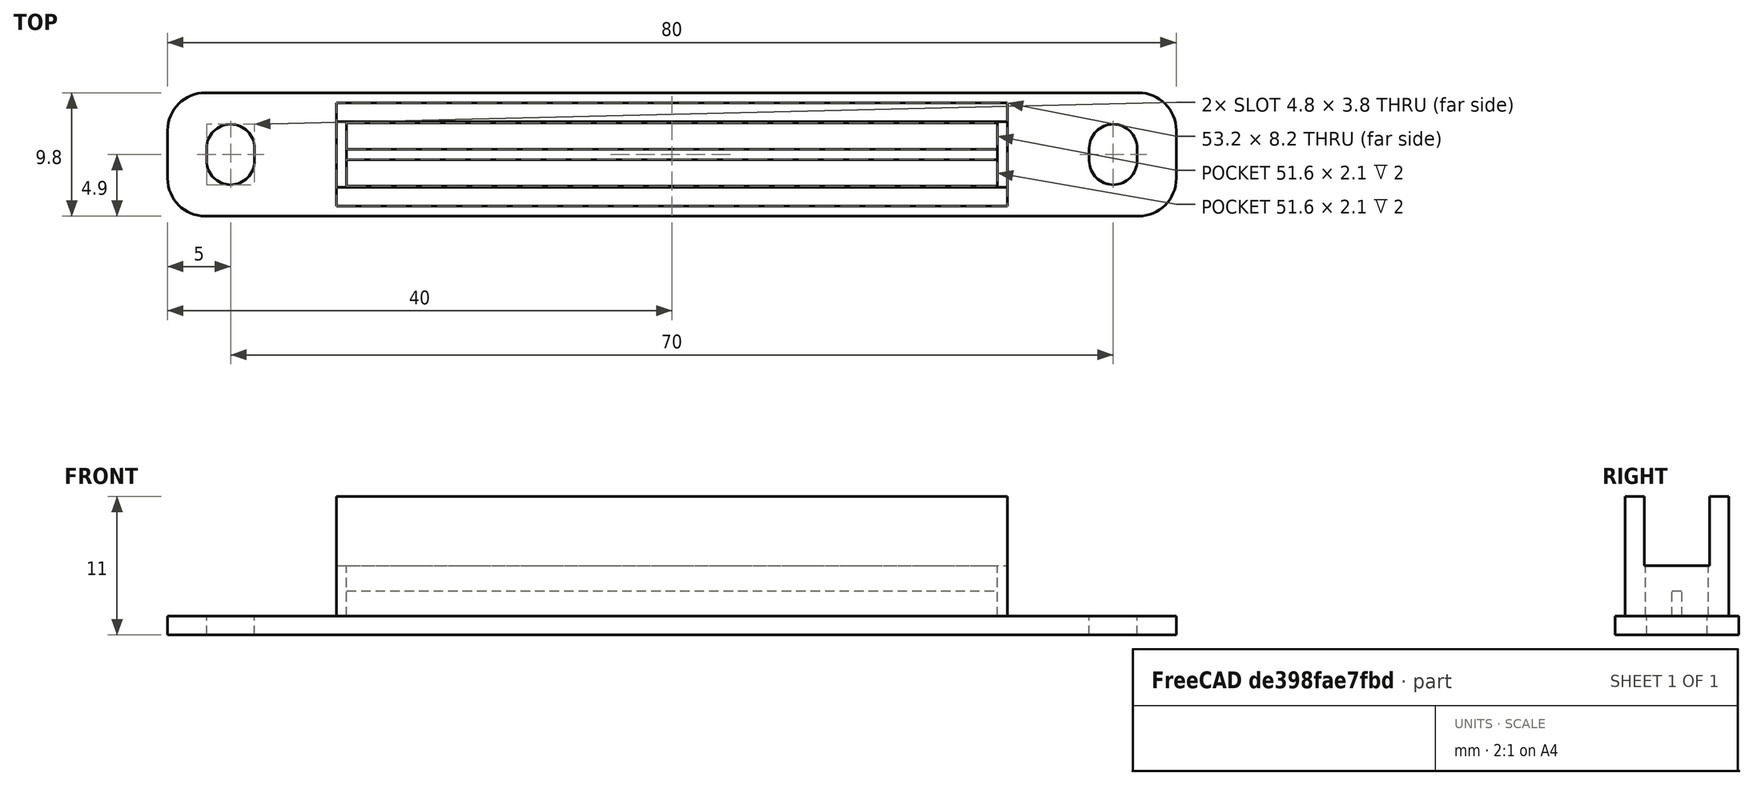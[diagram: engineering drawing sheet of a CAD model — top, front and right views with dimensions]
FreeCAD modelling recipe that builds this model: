
FCSTD DOCUMENT  (FreeCAD 0.19R23578 (Git))
Label: pin_socket_holder
License: All rights reserved
LicenseURL: http://en.wikipedia.org/wiki/All_rights_reserved
objects: Part::Box×6, Part::Cut×3, Part::MultiFuse×3, Spreadsheet::Sheet×2, Part::Cylinder×2, Part::Fillet×1, Part::FeaturePython×1
note: 16 computed .brp shape members not serialized (recipe doc carries the construction recipe); baked Part::Feature solids carry a one-line shape summary decoded from their .brp

FEATURE [Part::Box] Box  label="external cube"
  AttacherType = Attacher::AttachEngine3D
  Height = 11
  Length = 53.2
  Width = 8.2
  expr: Height = <<p>>.external_z
  expr: Width = <<p>>.internal_y + 2 * <<p>>.wall
  expr: Length = <<p>>.internal_x
FEATURE [Spreadsheet::Sheet] Spreadsheet  label="p"
  cells = A1=pin_step; B1(pin_step)==2.5mm; A2=pin_count_y; B2(pin_count_y)=2; A3=pin_count_x; B3(pin_count_x)=20; A4=wall; B4(wall)==1.5mm; A5=external_z; B5(external_z)==11mm; A6=internal_x; B6(internal_x)==pin_count_x * pin_step + 3.2mm; A7=internal_y; B7(internal_y)==pin_step * pin_count_y + 0.2mm; A8=internal_hole_x; B8(internal_hole_x)==pin_count_x * pin_step + 1.6mm; A9=internal_hole_y; B9(internal_hole_y)==pin_step * pin_count_y; A10=internal_hole_z; B10(internal_hole_z)==4mm; A11=hole_middle_extract_y; B11(hole_middle_extract_y)==0.8mm; A12=hole_middle_extract_z; B12(hole_middle_extract_z)==2mm
FEATURE [Part::Box] Box001  label="bottom hole"
  AttacherType = Attacher::AttachEngine3D
  Height = 4
  Length = 51.6
  Placement = pos=(0.8,1.6,1.5) rot=(0,0,1;0rad)
  Width = 5
  expr: Length = <<p>>.internal_hole_x
  expr: Width = <<p>>.internal_hole_y
  expr: Height = <<p>>.internal_hole_z
  expr: .Placement.Base.x = (<<external cube>>.Length - Length) / 2
  expr: .Placement.Base.y = (<<external cube>>.Width - Width) / 2
  expr: .Placement.Base.z = <<p>>.wall
FEATURE [Part::Box] Box002  label="internal_extraction"
  AttacherType = Attacher::AttachEngine3D
  Height = 11
  Length = 53.2
  Placement = pos=(0,1.5,5.5) rot=(0,0,1;0rad)
  Width = 5.2
  expr: Height = <<p>>.external_z
  expr: Length = <<p>>.internal_x
  expr: Width = <<p>>.internal_y
  expr: .Placement.Base.x = (<<external cube>>.Length - Length) / 2
  expr: .Placement.Base.y = (<<external cube>>.Width - Width) / 2
  expr: .Placement.Base.z = <<p>>.wall + <<p>>.internal_hole_z
FEATURE [Part::Box] Box003  label="bottom hole middle extraction"
  AttacherType = Attacher::AttachEngine3D
  Height = 2
  Length = 51.6
  Placement = pos=(0.8,3.7,1.5) rot=(0,0,1;0rad)
  Width = 0.8
  expr: .Placement.Base.z = <<p>>.wall
  expr: .Placement.Base.y = (<<external cube>>.Width - Width) / 2
  expr: .Placement.Base.x = (<<external cube>>.Length - Length) / 2
  expr: Width = <<p>>.hole_middle_extract_y
  expr: Length = <<p>>.internal_hole_x
  expr: Height = <<p>>.hole_middle_extract_z
FEATURE [Part::Cut] Cut003003  label="bottom hole cut"
  Base = -> Box001
  Tool = -> Box003
FEATURE [Part::MultiFuse] Fusion  label="hole fusion"
  Shapes = -> [Box002,Cut003003]
FEATURE [Part::Box] Box008  label="inbetween holes cube001"
  AttacherType = Attacher::AttachEngine3D
  Height = 10
  Length = 3.8
  Placement = pos=(-1.9,0,0) rot=(0,0,1;0rad)
  Width = 1
  expr: Length = <<attach_p>>.attach_hole_r * 2
  expr: .Placement.Base.x = -<<attach_p>>.attach_hole_r
  expr: Width = <<attach_p>>.attach_extra_width
FEATURE [Spreadsheet::Sheet] Spreadsheet001  label="attach_p"
  cells = A1=attach_hole_dist; B1(attach_hole_dist)==10mm; A2=attach_hole_r; B2(attach_hole_r)==1.9mm; A3=attach_hole_wall; B3(attach_hole_wall)==2.5mm; A4=attach_z; B4(attach_z)==1.5mm; A5=attach_box_x; B5(attach_box_x)==<<p>>.internal_x; A6=attach_box_y; B6(attach_box_y)==<<p>>.internal_y + <<p>>.wall * 2; A7=attach_extra_width; B7(attach_extra_width)==1mm; A8=attach_box_outside_space_count; B8(attach_box_outside_space_count)=3
FEATURE [Part::Cylinder] Cylinder004  label="attach hole003"
  Angle = 360
  AttacherType = Attacher::AttachEngine3D
  Height = 10
  Placement = pos=(0,1,0) rot=(0,0,1;0rad)
  Radius = 1.9
  expr: Radius = <<attach_p>>.attach_hole_r
  expr: .Placement.Base.y = <<attach_p>>.attach_extra_width
FEATURE [Part::Box] Box006  label="ears cube001"
  AttacherType = Attacher::AttachEngine3D
  Height = 1.5
  Length = 80
  Width = 9.8
  expr: Width = (<<attach_p>>.attach_hole_r + <<attach_p>>.attach_hole_wall) * 2 + <<attach_p>>.attach_extra_width
  expr: Length = floor(<<attach_p>>.attach_box_x / <<attach_p>>.attach_hole_dist + <<attach_p>>.attach_box_outside_space_count) * <<attach_p>>.attach_hole_dist
  expr: Height = <<attach_p>>.attach_z
FEATURE [Part::Fillet] Fillet003  label="ears cube fillet001"
  Base = -> Box006
  Edges = 4 edges r=3: [Edge1,Edge3,Edge5,Edge7]
FEATURE [Part::Cylinder] Cylinder002  label="attach hole001"
  Angle = 360
  AttacherType = Attacher::AttachEngine3D
  Height = 10
  Radius = 1.9
  expr: Radius = <<attach_p>>.attach_hole_r
FEATURE [Part::MultiFuse] Fusion002  label="attach hole fusion001"
  Placement = pos=(5,4.4,0) rot=(0,0,1;0rad)
  Shapes = -> [Cylinder004,Box008,Cylinder002]
  expr: .Placement.Base.x = <<attach_p>>.attach_hole_dist / 2
  expr: .Placement.Base.y = <<attach_p>>.attach_hole_r + <<attach_p>>.attach_hole_wall
FEATURE [Part::FeaturePython] Array003  label="attach hole array001"  # Draft array (typed FeaturePython)
  Angle = 360
  ArrayType = 0
  Axis = (0,0,1)
  Base = -> Fusion002
  Center = (0,0,0)
  Fuse = false
  IntervalAxis = (0,0,0)
  IntervalX = (70,0,0)
  IntervalY = (0,1,0)
  IntervalZ = (0,0,1)
  NumberPolar = 1
  NumberX = 2
  NumberY = 1
  NumberZ = 1
  expr: .IntervalX.x = floor(<<attach_p>>.attach_box_x / <<attach_p>>.attach_hole_dist + <<attach_p>>.attach_box_outside_space_count - 1) * <<attach_p>>.attach_hole_dist
FEATURE [Part::Cut] Cut003  label="attach plane x dir"
  Base = -> Fillet003
  Placement = pos=(-13.4,-0.8,0) rot=(0,0,1;0rad)
  Tool = -> Array003
  expr: .Placement.Base.x = -(floor(<<attach_p>>.attach_box_x / <<attach_p>>.attach_hole_dist + <<attach_p>>.attach_box_outside_space_count) * <<attach_p>>.attach_hole_dist - <<attach_p>>.attach_box_x) / 2
  expr: .Placement.Base.y = <<attach_p>>.attach_box_y / 2 - (<<attach_p>>.attach_hole_r + <<attach_p>>.attach_hole_wall + <<attach_p>>.attach_extra_width / 2)
FEATURE [Part::MultiFuse] Fusion001  label="body fusion"
  Shapes = -> [Box,Cut003]
FEATURE [Part::Cut] Cut  label="body cut"
  Base = -> Fusion001
  Tool = -> Fusion
